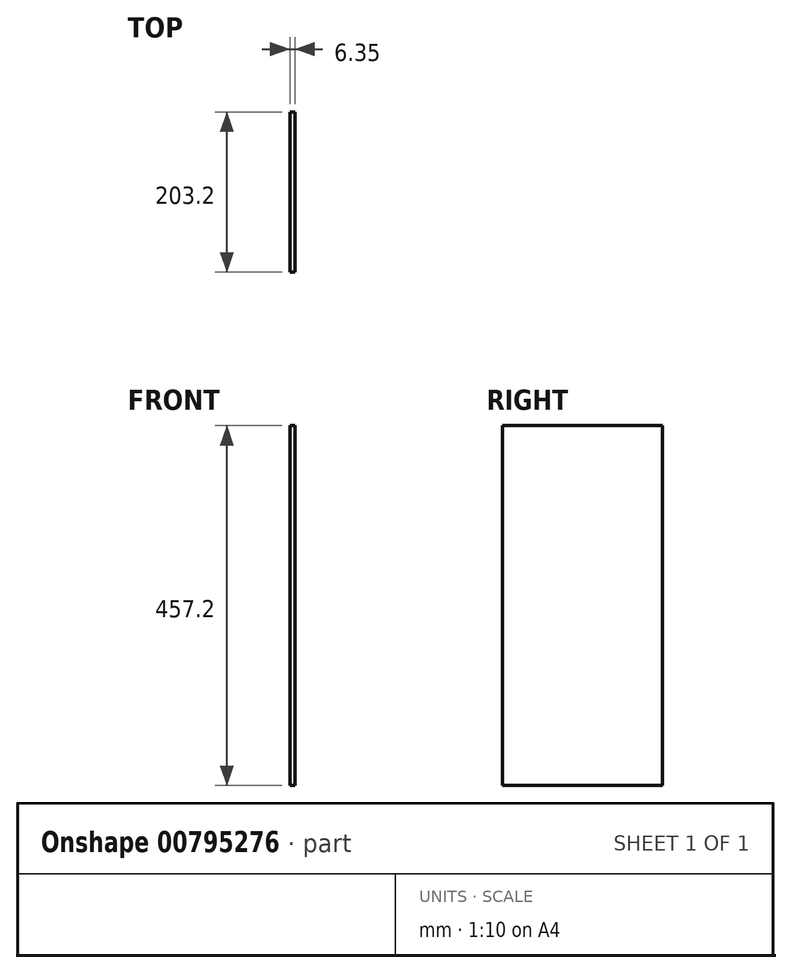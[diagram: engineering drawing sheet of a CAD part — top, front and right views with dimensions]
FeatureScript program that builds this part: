
annotation { "Feature Type Name" : "Feature", "Feature Type Description" : "" }
export const myFeature = defineFeature(function(context is Context, id is Id, definition is map)
    precondition{}
    {
        {
            var Q0;
            Q0=qCreatedBy(makeId("Right.planeOp"),FACE);
            var sketch = newSketch(context, id + "F0", { "sketchPlane" : qUnion([Q0])});
            skLineSegment(sketch, "E0.bottom", {"start": v(-101.6, -228.6) * mm, "end": v(101.6, -228.6) * mm});
            skLineSegment(sketch, "E0.top", {"start": v(-101.6, 228.6) * mm, "end": v(101.6, 228.6) * mm});
            skLineSegment(sketch, "E0.left", {"start": v(-101.6, -228.6) * mm, "end": v(-101.6, 228.6) * mm});
            skLineSegment(sketch, "E0.right", {"start": v(101.6, -228.6) * mm, "end": v(101.6, 228.6) * mm});
            skPoint(sketch, "E0.middle", {"position": v(0, 0) * mm});
            skSolve(sketch);
        }
        {
            var Q0;
            Q0=makeQuery(id+"F0.imprint","IMPRINT",FACE,{"disambiguationData":[TD([[makeQuery(id+"F0.imprint","IMPRINT",EDGE,{"derivedFrom":sQuery(id+"F0.wireOp",EDGE,"E0.bottom")}),1.0]])]});
            extrude(context, id + "F1", {"entities" : qUnion([Q0]), "depth" : 6.35 * mm, "offsetDistance" : 25.4 * mm});
        }
    });
